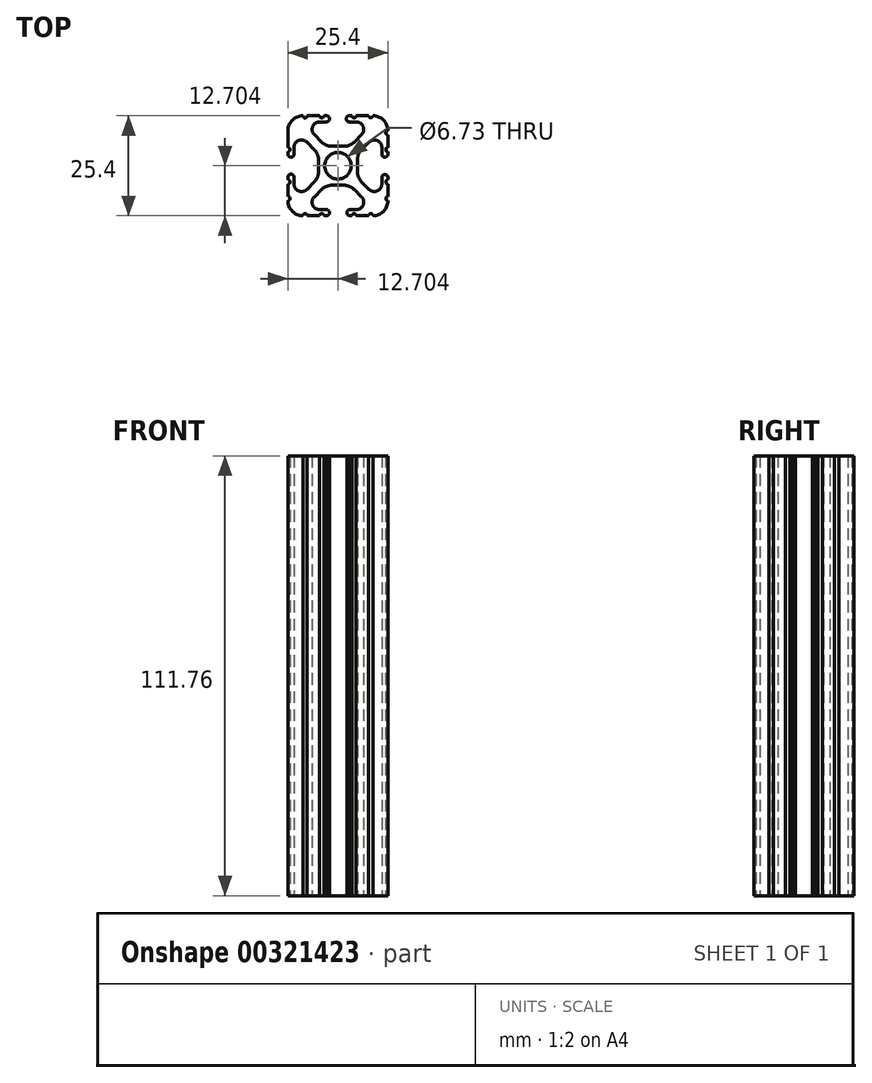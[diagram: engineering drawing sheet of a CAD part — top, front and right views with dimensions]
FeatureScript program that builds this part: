
annotation { "Feature Type Name" : "Feature", "Feature Type Description" : "" }
export const myFeature = defineFeature(function(context is Context, id is Id, definition is map)
    precondition{}
    {
        {
            var Q0;
            Q0=qCreatedBy(makeId("Top.planeOp"),FACE);
            var sketch = newSketch(context, id + "F0", { "sketchPlane" : qUnion([Q0])});
            skCircle(sketch, "E0", {"center": v(-0.59, -0.3) * mm, "radius": 3.36 * mm});
            skLineSegment(sketch, "E1.bottom", {"start": v(0.87, 4.63) * mm, "end": v(-2.04, 4.63) * mm});
            skLineSegment(sketch, "E1.top", {"start": v(0.87, -5.25) * mm, "end": v(-2.04, -5.25) * mm});
            skLineSegment(sketch, "E1.left", {"start": v(4.35, 1.15) * mm, "end": v(4.35, -1.76) * mm});
            skPoint(sketch, "E2.visualSharp", {"position": v(-13.29, 12.4) * mm});
            skPoint(sketch, "E3.visualSharp", {"position": v(12.11, 12.4) * mm});
            skPoint(sketch, "E4.visualSharp", {"position": v(12.11, -13) * mm});
            skPoint(sketch, "E5.visualSharp", {"position": v(-13.29, -13) * mm});
            skLineSegment(sketch, "E6.0", {"start": v(-6.58, 7.6) * mm, "end": v(-4.74, 5.75) * mm});
            skLineSegment(sketch, "E7.0", {"start": v(-8.49, 5.7) * mm, "end": v(-6.64, 3.85) * mm});
            skPoint(sketch, "E8.orphan", {"position": v(-11.74, -11.46) * mm});
            skPoint(sketch, "E9.orphan", {"position": v(-11.74, 10.85) * mm});
            skPoint(sketch, "E10.orphan", {"position": v(10.57, 10.85) * mm});
            skPoint(sketch, "E11.orphan", {"position": v(10.57, -11.46) * mm});
            skLineSegment(sketch, "E12", {"start": v(3.57, -6.36) * mm, "end": v(5.4, -8.2) * mm});
            skLineSegment(sketch, "E13.0", {"start": v(-6.58, -8.2) * mm, "end": v(-4.74, -6.36) * mm});
            skLineSegment(sketch, "E14.0", {"start": v(3.57, 5.75) * mm, "end": v(5.41, 7.6) * mm});
            skPoint(sketch, "E15.visualSharp", {"position": v(-11.74, 8.94) * mm});
            skArc(sketch, "E15.filletArc", {"start": v(-8.49, 5.7) * mm, "mid": v(-10.56, 6.1) * mm, "end": v(-11.74, 4.34) * mm});
            skPoint(sketch, "E16.visualSharp", {"position": v(-9.83, 10.85) * mm});
            skArc(sketch, "E16.filletArc", {"start": v(-5.24, 10.85) * mm, "mid": v(-7, 9.67) * mm, "end": v(-6.58, 7.6) * mm});
            skPoint(sketch, "E17.visualSharp", {"position": v(6.77, 10.85) * mm});
            skLineSegment(sketch, "E18", {"start": v(-5.24, 10.85) * mm, "end": v(-3.47, 10.85) * mm});
            skLineSegment(sketch, "E19", {"start": v(-11.74, 4.34) * mm, "end": v(-11.74, 2.6) * mm});
            skLineSegment(sketch, "E20", {"start": v(4.06, -11.46) * mm, "end": v(2.33, -11.46) * mm});
            skArc(sketch, "E21.filletArc", {"start": v(5.41, 7.6) * mm, "mid": v(5.82, 9.67) * mm, "end": v(4.06, 10.85) * mm});
            skPoint(sketch, "E22.visualSharp", {"position": v(10.57, -9.55) * mm});
            skPoint(sketch, "E23.visualSharp", {"position": v(8.66, -11.46) * mm});
            skArc(sketch, "E23.filletArc", {"start": v(4.06, -11.46) * mm, "mid": v(5.82, -10.28) * mm, "end": v(5.4, -8.2) * mm});
            skArc(sketch, "E24.filletArc", {"start": v(-6.58, -8.2) * mm, "mid": v(-7, -10.28) * mm, "end": v(-5.23, -11.46) * mm});
            skLineSegment(sketch, "E25.bottom", {"start": v(7.22, -13) * mm, "end": v(4.06, -13) * mm});
            skLineSegment(sketch, "E25.top", {"start": v(7.2, 12.4) * mm, "end": v(4.06, 12.4) * mm});
            skLineSegment(sketch, "E25.left", {"start": v(12.11, -8.1) * mm, "end": v(12.11, -4.95) * mm});
            skArc(sketch, "E26.filletArc", {"start": v(-13.29, -9.2) * mm, "mid": v(-12.17, -11.9) * mm, "end": v(-9.48, -13) * mm});
            skArc(sketch, "E27.filletArc", {"start": v(8.3, -13) * mm, "mid": v(11, -11.9) * mm, "end": v(12.11, -9.2) * mm});
            skArc(sketch, "E28.filletArc", {"start": v(12.11, 8.58) * mm, "mid": v(11, 11.28) * mm, "end": v(8.3, 12.4) * mm});
            skArc(sketch, "E29.filletArc", {"start": v(-9.48, 12.4) * mm, "mid": v(-12.17, 11.28) * mm, "end": v(-13.29, 8.58) * mm});
            skPoint(sketch, "E30.newPointA", {"position": v(-5.52, -5.25) * mm});
            skArc(sketch, "E30.filletArc", {"start": v(-2.04, -5.25) * mm, "mid": v(-3.5, -5.54) * mm, "end": v(-4.74, -6.36) * mm});
            skPoint(sketch, "E31.newPointA", {"position": v(4.35, -5.25) * mm});
            skArc(sketch, "E31.filletArc", {"start": v(3.57, -6.36) * mm, "mid": v(2.33, -5.54) * mm, "end": v(0.87, -5.25) * mm});
            skArc(sketch, "E32.filletArc", {"start": v(4.35, -1.76) * mm, "mid": v(4.64, -3.22) * mm, "end": v(5.47, -4.46) * mm});
            skArc(sketch, "E33.filletArc", {"start": v(5.47, 3.85) * mm, "mid": v(4.64, 2.6) * mm, "end": v(4.35, 1.15) * mm});
            skPoint(sketch, "E34.newPointB", {"position": v(4.35, 4.63) * mm});
            skArc(sketch, "E34.filletArc", {"start": v(0.87, 4.63) * mm, "mid": v(2.33, 4.92) * mm, "end": v(3.57, 5.75) * mm});
            skPoint(sketch, "E35.newPointB", {"position": v(-5.52, 4.63) * mm});
            skArc(sketch, "E35.filletArc", {"start": v(-4.74, 5.75) * mm, "mid": v(-3.5, 4.92) * mm, "end": v(-2.04, 4.63) * mm});
            skArc(sketch, "E36.filletArc", {"start": v(-5.52, 1.15) * mm, "mid": v(-5.81, 2.6) * mm, "end": v(-6.64, 3.85) * mm});
            skLineSegment(sketch, "E37.filletArc", {"start": v(-5.52, -6.57) * mm, "end": v(-5.52, -6.57) * mm});
            skLineSegment(sketch, "E38", {"start": v(5.47, -4.46) * mm, "end": v(7.31, -6.3) * mm});
            skPoint(sketch, "E39.visualSharp", {"position": v(10.57, 8.94) * mm});
            skArc(sketch, "E40.filletArc", {"start": v(7.31, -6.3) * mm, "mid": v(9.39, -6.71) * mm, "end": v(10.57, -4.95) * mm});
            skLineSegment(sketch, "E41", {"start": v(10.57, -4.95) * mm, "end": v(10.57, -3.22) * mm});
            skLineSegment(sketch, "E42", {"start": v(5.47, 3.85) * mm, "end": v(7.31, 5.69) * mm});
            skArc(sketch, "E43.filletArc", {"start": v(10.57, 4.34) * mm, "mid": v(9.39, 6.1) * mm, "end": v(7.31, 5.69) * mm});
            skArc(sketch, "E44", {"start": v(-11.74, -3.22) * mm, "mid": v(-12.51, -2.45) * mm, "end": v(-13.29, -3.22) * mm});
            skArc(sketch, "E45", {"start": v(-13.29, 2.6) * mm, "mid": v(-12.51, 1.85) * mm, "end": v(-11.74, 2.6) * mm});
            skArc(sketch, "E46", {"start": v(-3.5, 10.85) * mm, "mid": v(-2.71, 11.62) * mm, "end": v(-3.5, 12.4) * mm});
            skArc(sketch, "E47", {"start": v(2.33, 12.4) * mm, "mid": v(1.52, 11.62) * mm, "end": v(2.33, 10.85) * mm});
            skArc(sketch, "E48", {"start": v(10.57, 2.6) * mm, "mid": v(11.34, 1.87) * mm, "end": v(12.11, 2.6) * mm});
            skArc(sketch, "E49", {"start": v(12.11, -3.22) * mm, "mid": v(11.34, -2.5) * mm, "end": v(10.57, -3.22) * mm});
            skArc(sketch, "E50", {"start": v(2.33, -11.46) * mm, "mid": v(1.71, -12.23) * mm, "end": v(2.33, -13) * mm});
            skArc(sketch, "E51", {"start": v(-3.5, -13) * mm, "mid": v(-2.74, -12.23) * mm, "end": v(-3.5, -11.46) * mm});
            skLineSegment(sketch, "E52.trimOffspring", {"start": v(-3.5, -11.46) * mm, "end": v(-5.23, -11.46) * mm});
            skLineSegment(sketch, "E53.trimOffspring", {"start": v(10.57, 2.6) * mm, "end": v(10.57, 4.34) * mm});
            skLineSegment(sketch, "E54.trimOffspring", {"start": v(12.11, 2.6) * mm, "end": v(12.11, 3.25) * mm});
            skLineSegment(sketch, "E55.trimOffspring", {"start": v(-13.29, 2.6) * mm, "end": v(-13.29, 3.25) * mm});
            skLineSegment(sketch, "E56.trimOffspring", {"start": v(2.26, 10.85) * mm, "end": v(4.06, 10.85) * mm});
            skLineSegment(sketch, "E57.trimOffspring", {"start": v(-3.47, 12.4) * mm, "end": v(-4.14, 12.4) * mm});
            skPoint(sketch, "E58.start.orphan", {"position": v(-3.5, 4.92) * mm});
            skPoint(sketch, "E59.start.orphan", {"position": v(2.33, 4.92) * mm});
            skPoint(sketch, "E60.start.orphan", {"position": v(4.64, 2.6) * mm});
            skPoint(sketch, "E61.start.orphan", {"position": v(4.64, -3.22) * mm});
            skPoint(sketch, "E62.start.orphan", {"position": v(-5.81, 2.6) * mm});
            skPoint(sketch, "E63.start.orphan", {"position": v(-5.52, -6.57) * mm});
            skPoint(sketch, "E64.start.orphan", {"position": v(2.33, -5.54) * mm});
            skPoint(sketch, "E65.start.orphan", {"position": v(-3.5, -5.54) * mm});
            skPoint(sketch, "E66.endSnap0", {"position": v(12.11, 5.6) * mm});
            skPoint(sketch, "E67.startSnap0", {"position": v(10.57, -4.09) * mm});
            skArc(sketch, "E68", {"start": v(7.2, 12.4) * mm, "mid": v(7.75, 11.9) * mm, "end": v(8.3, 12.4) * mm});
            skArc(sketch, "E69", {"start": v(2.97, 12.4) * mm, "mid": v(3.52, 11.85) * mm, "end": v(4.06, 12.4) * mm});
            skArc(sketch, "E70", {"start": v(-5.24, 12.4) * mm, "mid": v(-4.69, 11.85) * mm, "end": v(-4.14, 12.4) * mm});
            skArc(sketch, "E71", {"start": v(-9.48, 12.4) * mm, "mid": v(-8.92, 11.84) * mm, "end": v(-8.37, 12.4) * mm});
            skLineSegment(sketch, "E72", {"start": v(-13.29, 8.58) * mm, "end": v(-13.29, 7.5) * mm});
            skArc(sketch, "E73", {"start": v(-13.29, 3.25) * mm, "mid": v(-12.73, 3.8) * mm, "end": v(-13.29, 4.34) * mm});
            skArc(sketch, "E74", {"start": v(-13.29, -9.2) * mm, "mid": v(-12.73, -8.65) * mm, "end": v(-13.29, -8.1) * mm});
            skArc(sketch, "E75", {"start": v(-8.38, -13) * mm, "mid": v(-8.93, -12.45) * mm, "end": v(-9.48, -13) * mm});
            skArc(sketch, "E76", {"start": v(4.06, -13) * mm, "mid": v(3.51, -12.46) * mm, "end": v(2.96, -13) * mm});
            skArc(sketch, "E77", {"start": v(8.3, -13) * mm, "mid": v(7.76, -12.46) * mm, "end": v(7.22, -13) * mm});
            skLineSegment(sketch, "E78.trimOffspring", {"start": v(-5.24, 12.4) * mm, "end": v(-8.37, 12.4) * mm});
            skLineSegment(sketch, "E79.trimOffspring", {"start": v(-13.29, 4.34) * mm, "end": v(-13.29, 8.58) * mm});
            skLineSegment(sketch, "E80.trimOffspring", {"start": v(-13.29, -3.86) * mm, "end": v(-13.29, -3.22) * mm});
            skLineSegment(sketch, "E81.trimOffspring", {"start": v(2.96, -13) * mm, "end": v(2.33, -13) * mm});
            skArc(sketch, "E82", {"start": v(12.11, -8.1) * mm, "mid": v(11.58, -8.65) * mm, "end": v(12.11, -9.2) * mm});
            skArc(sketch, "E83", {"start": v(12.11, -3.86) * mm, "mid": v(11.57, -4.4) * mm, "end": v(12.11, -4.95) * mm});
            skLineSegment(sketch, "E84.trimOffspring", {"start": v(12.11, -3.86) * mm, "end": v(12.11, -3.22) * mm});
            skArc(sketch, "E85", {"start": v(12.11, 8.58) * mm, "mid": v(11.56, 8.04) * mm, "end": v(12.11, 7.49) * mm});
            skArc(sketch, "E86", {"start": v(12.11, 4.34) * mm, "mid": v(11.57, 3.8) * mm, "end": v(12.11, 3.25) * mm});
            skLineSegment(sketch, "E87.trimOffspring", {"start": v(12.11, 4.34) * mm, "end": v(12.11, 7.49) * mm});
            skLineSegment(sketch, "E88.trimOffspring", {"start": v(2.97, 12.4) * mm, "end": v(2.26, 12.4) * mm});
            skPoint(sketch, "E89.1.0", {"position": v(15.19, -0.3) * mm});
            skPoint(sketch, "E89.1.3", {"position": v(5.17, -1.94) * mm});
            skPoint(sketch, "E89.1.9", {"position": v(13.84, 1.04) * mm});
            skPoint(sketch, "E89.1.13", {"position": v(13.84, -1.65) * mm});
            skPoint(sketch, "E89.1.17", {"position": v(17.37, -0.3) * mm});
            skPoint(sketch, "E89.1.19", {"position": v(17.37, -0.3) * mm});
            skArc(sketch, "E89.2.1", {"start": v(-13.29, -9.2) * mm, "mid": v(-12.73, -8.64) * mm, "end": v(-13.29, -8.1) * mm});
            skPoint(sketch, "E89.2.3", {"position": v(-5.81, -3.22) * mm});
            skLineSegment(sketch, "E89.2.4", {"start": v(-11.74, -4.96) * mm, "end": v(-11.74, -3.19) * mm});
            skLineSegment(sketch, "E89.2.5", {"start": v(-5.24, -11.46) * mm, "end": v(-3.5, -11.46) * mm});
            skLineSegment(sketch, "E89.2.6", {"start": v(-8.49, -6.3) * mm, "end": v(-6.64, -4.46) * mm});
            skArc(sketch, "E89.2.7", {"start": v(-6.58, -8.2) * mm, "mid": v(-7, -10.28) * mm, "end": v(-5.24, -11.46) * mm});
            skArc(sketch, "E89.2.8", {"start": v(-11.74, -4.96) * mm, "mid": v(-10.56, -6.72) * mm, "end": v(-8.49, -6.3) * mm});
            skPoint(sketch, "E89.2.9", {"position": v(-9.83, -11.46) * mm});
            skArc(sketch, "E89.2.10", {"start": v(-4.14, -13) * mm, "mid": v(-4.69, -12.45) * mm, "end": v(-5.24, -13) * mm});
            skLineSegment(sketch, "E89.2.11", {"start": v(-13.29, -4.96) * mm, "end": v(-13.29, -8.1) * mm});
            skArc(sketch, "E89.2.12", {"start": v(-3.5, -13) * mm, "mid": v(-2.75, -12.23) * mm, "end": v(-3.5, -11.46) * mm});
            skPoint(sketch, "E89.2.13", {"position": v(-11.74, -9.56) * mm});
            skArc(sketch, "E89.2.15", {"start": v(-11.74, -3.22) * mm, "mid": v(-12.51, -2.43) * mm, "end": v(-13.29, -3.22) * mm});
            skArc(sketch, "E89.2.16", {"start": v(-13.29, -4.96) * mm, "mid": v(-12.74, -4.4) * mm, "end": v(-13.29, -3.86) * mm});
            skLineSegment(sketch, "E89.2.20", {"start": v(-3.5, -13) * mm, "end": v(-4.14, -13) * mm});
            skLineSegment(sketch, "E89.2.21", {"start": v(-13.29, -3.19) * mm, "end": v(-13.29, -3.86) * mm});
            skArc(sketch, "E89.2.24", {"start": v(-6.64, -4.46) * mm, "mid": v(-5.81, -3.22) * mm, "end": v(-5.52, -1.76) * mm});
            skLineSegment(sketch, "E89.anchor1", {"start": v(-0.59, -0.3) * mm, "end": v(-13.29, 2.6) * mm, "construction": true});
            skLineSegment(sketch, "E89.anchor2", {"start": v(-0.59, -0.3) * mm, "end": v(-3.5, -13) * mm, "construction": true});
            skLineSegment(sketch, "E90", {"start": v(-8.38, -13) * mm, "end": v(-5.24, -13) * mm});
            skLineSegment(sketch, "E91", {"start": v(-5.52, -1.76) * mm, "end": v(-5.52, 1.15) * mm});
            skSolve(sketch);
        }
        {
            var Q0;
            Q0=makeQuery(id+"F0.imprint","IMPRINT",FACE,{"disambiguationData":[TD([[makeQuery(id+"F0.imprint","IMPRINT",EDGE,{"derivedFrom":sQuery(id+"F0.wireOp",EDGE,"E0")}),-1.0]])]});
            extrude(context, id + "F1", {"entities" : qUnion([Q0]), "depth" : 111.76 * mm});
        }
    });
